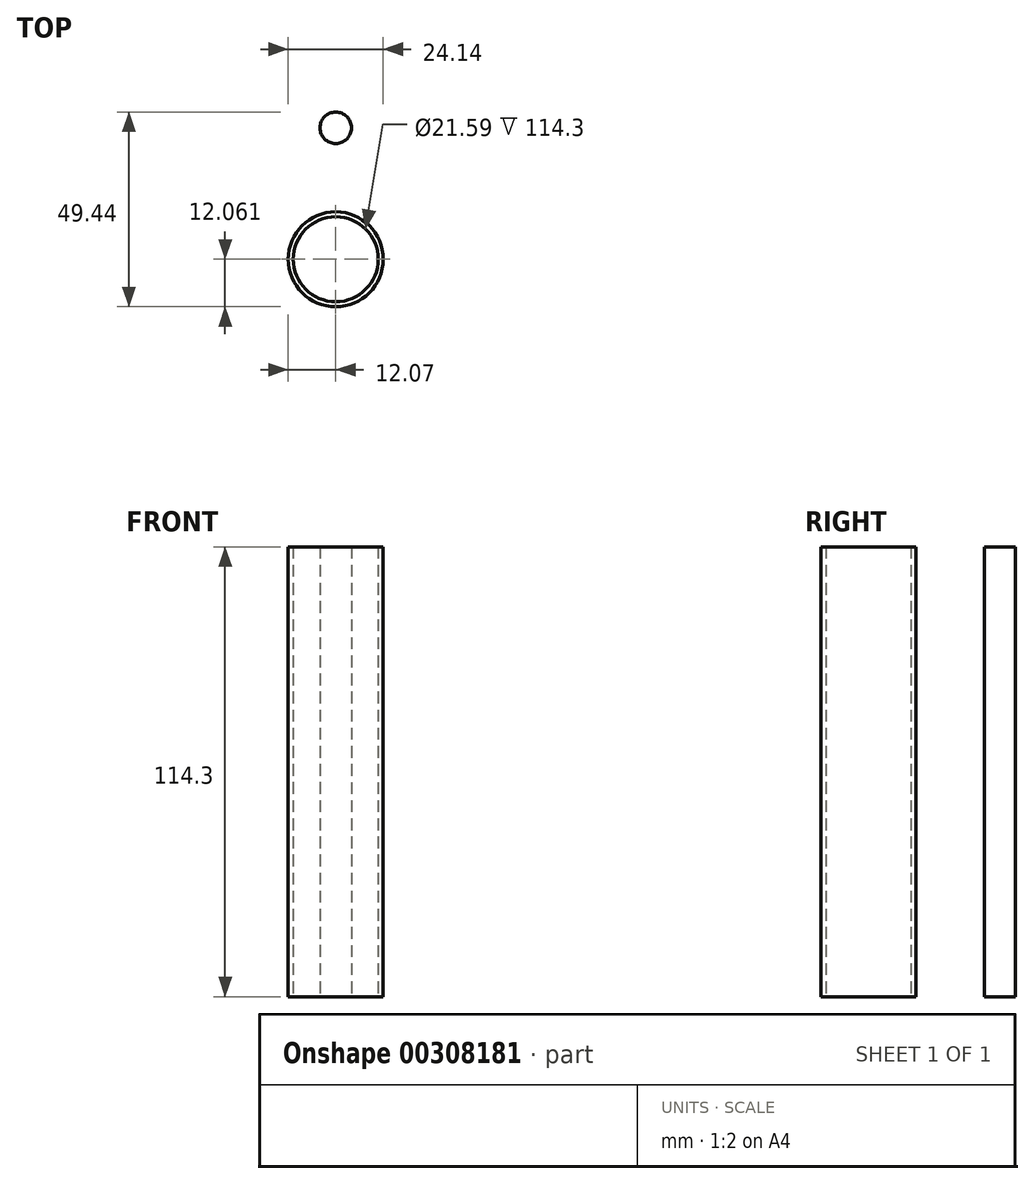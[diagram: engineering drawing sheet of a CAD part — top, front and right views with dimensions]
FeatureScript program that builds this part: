
annotation { "Feature Type Name" : "Feature", "Feature Type Description" : "" }
export const myFeature = defineFeature(function(context is Context, id is Id, definition is map)
    precondition{}
    {
        {
            var Q0;
            Q0=qCreatedBy(makeId("Top.planeOp"),FACE);
            var sketch = newSketch(context, id + "F0", { "sketchPlane" : qUnion([Q0])});
            skCircle(sketch, "E0", {"center": v(0, -11.13) * mm, "radius": 12.07 * mm});
            skCircle(sketch, "E1", {"center": v(0, -11.13) * mm, "radius": 10.8 * mm});
            skCircle(sketch, "E2", {"center": v(0, 22.26) * mm, "radius": 3.99 * mm});
            skSolve(sketch);
        }
        {
            var Q0;
            Q0=makeQuery(id+"F0.imprint","IMPRINT",FACE,{"disambiguationData":[TD([[makeQuery(id+"F0.imprint","IMPRINT",EDGE,{"derivedFrom":sQuery(id+"F0.wireOp",EDGE,"E2")}),1.0]])]});
            extrude(context, id + "F1", {"entities" : qUnion([Q0]), "depth" : 107.95 * mm});
        }
        {
            var Q0;
            Q0 = qSketchRegion(id + "F0", true);
            var Q1;
            Q1=makeQuery(id+"F1.opExtrude","CAP_FACE",FACE,{"disambiguationData":[OSD([sQuery(id+"F0.wireOp",EDGE,"E2")])],"isStart":true});
            extrude(context, id + "F2", {"entities" : qUnion([Q0, Q1]), "operationType" : NewBodyOperationType.ADD, "depth" : 114.3 * mm});
        }
    });
